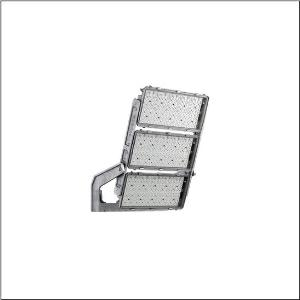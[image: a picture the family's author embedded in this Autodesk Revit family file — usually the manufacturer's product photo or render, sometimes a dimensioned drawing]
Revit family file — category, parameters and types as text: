
# Revit family: floodlight_fl_11_maxi_pro_remote___pl52_5xa779426d01ba_5366
name_source: partatom
category: Lighting Fixtures
units: mm (PartAtom-declared; Revit-internal decimal feet)

## family parameters
Cut with Voids When Loaded = No
Host = Face
Light Source = No
Part Type = Normal
Room Calculation Point = No
Round Connector Dimension = Use Diameter
Shared = No

## types (1)
- --- (1 x LED, 146220 lm, 1095.8 W, 4000K)
    Apparent Load = 1096 VA
    CIE Flux Codes = 24 55 98 100 100
    Color Rendering = 70
    Color Temperature = 4000K
    Default Elevation = 1800 mm
    Description = Floodlight FL 11  maxi  pro Remote floodlight; light control with lens of PMMA; cover panel of toughened safety glass, transparent; light distribution: PL52, asymmetric direct distribution, LEDcolour temperature: 4000K, rated luminous flux: 146.220lm, colour rendering: CRI > 70, light colour: 740; luminous efficacy: 133lm/W; brightness control: DALI 2 (1 DALI address); with terminal, 8-pole, max. 2.5mm², mains connection: 220..240V/380..400V AC, 50/60Hz, surge voltage resistance: line to ground: 10kV, ECG replaceable separately, LED unit replaceable without ESD environment, dustproof LED module, dimming range 10..100%, no afterglow with DALI off / DMX off command; 1096W floodlight with 3x LED unit of diecast aluminium, coated grey; length: 713mm / width: 651mm / height: 338mm; mounting bracket, of diecast aluminium, uncoated, natural, equipment: Longlife, protection rating (complete): IP66; insulation class (complete): insulation class I (protective earthing); certification: CE, ENEC, VDE; ball protection: ball impact resistance with accessories, impact resistance: IK07; rated ambient temperature 10°C, only for outdoor installations, permissible operating ambient temperature: -40..+40°C, permissible storage temperature: -40..+85°C; packaging unit: 1 piece

Light Distribution: PL52
    Height = 320 mm
    Lamp = 1 x LED
    Lamp Light Flux = 146220 lm
    Lamp Power = 1095.8 W
    Lamp count = 1
    Length = 1002 mm
    Luminous efficacy = 133 lm/W
    Manufacturer = Siteco
    ModVariant = No
    Model = 5XA779426D01BA
    Mounting Place = Ceiling
    Mounting Type = Surface mounted
    Number of Poles = 1
    OnlyDefault = Yes
    Power Factor = 1
    Product Name = Floodlight FL 11 maxi pro Remote | PL52
    Product group = floodlight | ceiling mounted
    ProductGroupID = 302
    Protection Class = Protection class I
    Protection Degree = IP 66
    RLX_Detail_Level = 1
    RLX_Emergency_Light_Flux = 0 lm
    RLX_Emergency_Type = 0
    RLX_Emergency_Type_DB = No
    RlxData = <blob elided: 52465 chars, md5=7624d41e>
    Socket = socket
    Standby Power = 0 W
    System Light Flux = 146220 lm
    System Power = 1096 W
    Type Comments = factory setting: luminous flux: 100 % | dim-lin: 254 | 760 mA
    Type Image = l_1006784.jpg
    URL = http://relux.com
    VarID = @adj_028149
    Voltage = 0 V
    Weight = 0.00 kg
    Width = 655 mm

## geometry (parser evidence)
native form markers: Blend x4, Sweep x13
no freeform markers — native parametric forms only
